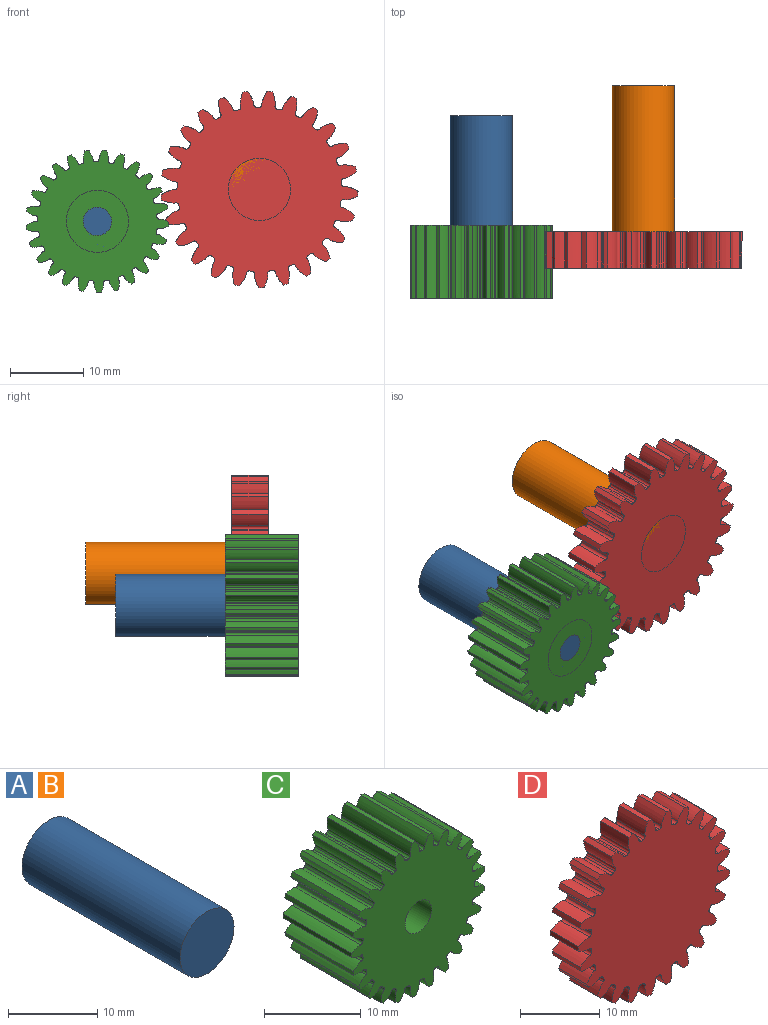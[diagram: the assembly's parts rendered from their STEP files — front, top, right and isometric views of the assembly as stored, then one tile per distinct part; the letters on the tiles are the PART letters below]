
ASSEMBLY  parts=4 mates=2
PART A: 3 faces, bbox 8.5x25x8.5 mm
  f0: cylinder r=4.26mm len=25mm, axis (0,1,0), area 669.3mm2, adj f1,f2
  f1: plane 8.52x8.52mm, normal (0,-1,0), area 57mm2, adj f0
  f2: plane 8.52x8.52mm, normal (0,1,0), area 57mm2, adj f0
PART B: same geometry as A
PART C: 153 faces, bbox 19.5x10x19.6 mm
  f0: cylinder r=9.8mm len=10mm, axis (0,1,0), area 5.2mm2, adj f24,f26,f137,f149
  f1: cylinder r=9.8mm len=10mm, axis (0,1,0), area 5.2mm2, adj f24,f26,f144,f147
  f2: cylinder r=9.8mm len=10mm, axis (0,1,0), area 5.2mm2, adj f24,f26,f132,f139
  f3: cylinder r=9.8mm len=10mm, axis (0,1,0), area 5.2mm2, adj f24,f26,f127,f134
  f4: cylinder r=9.8mm len=10mm, axis (0,1,0), area 5.2mm2, adj f24,f26,f122,f129
  f5: cylinder r=9.8mm len=10mm, axis (0,1,0), area 5.2mm2, adj f24,f26,f112,f124
  f6: cylinder r=9.8mm len=10mm, axis (0,1,0), area 5.2mm2, adj f24,f26,f107,f119
  f7: cylinder r=9.8mm len=10mm, axis (0,1,0), area 5.2mm2, adj f24,f26,f114,f117
  f8: cylinder r=9.8mm len=10mm, axis (0,1,0), area 5.2mm2, adj f24,f26,f102,f109
  f9: cylinder r=9.8mm len=10mm, axis (0,1,0), area 5.2mm2, adj f24,f26,f97,f104
  f10: cylinder r=9.8mm len=10mm, axis (0,1,0), area 5.2mm2, adj f24,f26,f92,f99
  f11: cylinder r=9.8mm len=10mm, axis (0,1,0), area 5.2mm2, adj f24,f26,f77,f94
  f12: cylinder r=9.8mm len=10mm, axis (0,1,0), area 5.2mm2, adj f24,f26,f27,f89
  f13: cylinder r=9.8mm len=10mm, axis (0,1,0), area 5.2mm2, adj f24,f26,f84,f87
  f14: cylinder r=9.8mm len=10mm, axis (0,1,0), area 5.2mm2, adj f24,f26,f72,f79
  f15: cylinder r=9.8mm len=10mm, axis (0,1,0), area 5.2mm2, adj f24,f26,f74,f82
  f16: cylinder r=9.8mm len=10mm, axis (0,1,0), area 5.2mm2, adj f24,f26,f69,f142
  f17: cylinder r=9.8mm len=10mm, axis (0,1,0), area 5.2mm2, adj f24,f26,f64,f67
  f18: cylinder r=9.8mm len=10mm, axis (0,1,0), area 5.2mm2, adj f24,f26,f59,f62
  f19: cylinder r=9.8mm len=10mm, axis (0,1,0), area 5.2mm2, adj f24,f26,f54,f57
  f20: cylinder r=9.8mm len=10mm, axis (0,1,0), area 5.2mm2, adj f24,f26,f42,f49
  f21: cylinder r=9.8mm len=10mm, axis (0,1,0), area 5.2mm2, adj f24,f26,f32,f44
  f22: cylinder r=9.8mm len=10mm, axis (0,1,0), area 5.2mm2, adj f24,f26,f39,f52
  f23: cylinder r=9.8mm len=10mm, axis (0,1,0), area 5.2mm2, adj f24,f26,f34,f37
  f24: plane 19.59x19.55mm, normal (0,-1,0), area 242.9mm2, adj f0,f1,f2,f3,f4,f5,f6,f7
  f25: cylinder r=9.8mm len=10mm, axis (0,1,0), area 5.2mm2, adj f24,f26,f29,f47
  f26: plane 19.59x19.55mm, normal (0,1,0), area 242.9mm2, adj f0,f1,f2,f3,f4,f5,f6,f7
  f27: extruded ~10x1.32mm, area 14.6mm2, adj f12,f24,f26,f30
  f28: cylinder r=8.16mm len=10mm, axis (0,1,0), area 2.5mm2, adj f24,f26,f30,f31
  f29: extruded ~10x1.32mm, area 14.6mm2, adj f24,f25,f26,f31
  f30: cylinder r=0.27mm len=10mm, axis (0,1,0), area 4.2mm2, adj f24,f26,f27,f28
  f31: cylinder r=0.27mm len=10mm, axis (0,1,0), area 4.2mm2, adj f24,f26,f28,f29
  f32: extruded ~10x1.35mm, area 14.6mm2, adj f21,f24,f26,f35
  f33: cylinder r=8.16mm len=10mm, axis (0,1,0), area 2.5mm2, adj f24,f26,f35,f36
  f34: extruded ~10x1.32mm, area 14.6mm2, adj f23,f24,f26,f36
  f35: cylinder r=0.27mm len=10mm, axis (0,1,0), area 4.2mm2, adj f24,f26,f32,f33
  f36: cylinder r=0.27mm len=10mm, axis (0,1,0), area 4.2mm2, adj f24,f26,f33,f34
  f37: extruded ~10x1.19mm, area 14.6mm2, adj f23,f24,f26,f40
  f38: cylinder r=8.16mm len=10mm, axis (0,1,0), area 2.5mm2, adj f24,f26,f40,f41
  f39: extruded ~10x1.42mm, area 14.6mm2, adj f22,f24,f26,f41
  f40: cylinder r=0.27mm len=10mm, axis (0,1,0), area 4.2mm2, adj f24,f26,f37,f38
  f41: cylinder r=0.27mm len=10mm, axis (0,1,0), area 4.2mm2, adj f24,f26,f38,f39
  f42: extruded ~10x1.43mm, area 14.6mm2, adj f20,f24,f26,f45
  f43: cylinder r=8.16mm len=10mm, axis (0,1,0), area 2.5mm2, adj f24,f26,f45,f46
  f44: extruded ~10x1.13mm, area 14.6mm2, adj f21,f24,f26,f46
  f45: cylinder r=0.27mm len=10mm, axis (0,1,0), area 4.2mm2, adj f24,f26,f42,f43
  f46: cylinder r=0.27mm len=10mm, axis (0,1,0), area 4.2mm2, adj f24,f26,f43,f44
  f47: extruded ~10x1.42mm, area 14.6mm2, adj f24,f25,f26,f50
  f48: cylinder r=8.16mm len=10mm, axis (0,1,0), area 2.5mm2, adj f24,f26,f50,f51
  f49: extruded ~10x1.14mm, area 14.6mm2, adj f20,f24,f26,f51
  f50: cylinder r=0.27mm len=10mm, axis (0,1,0), area 4.2mm2, adj f24,f26,f47,f48
  f51: cylinder r=0.27mm len=10mm, axis (0,1,0), area 4.2mm2, adj f24,f26,f48,f49
  f52: extruded ~10x1.09mm, area 14.6mm2, adj f22,f24,f26,f55
  f53: cylinder r=8.16mm len=10mm, axis (0,1,0), area 2.5mm2, adj f24,f26,f55,f56
  f54: extruded ~10x1.43mm, area 14.6mm2, adj f19,f24,f26,f56
  f55: cylinder r=0.27mm len=10mm, axis (0,1,0), area 4.2mm2, adj f24,f26,f52,f53
  f56: cylinder r=0.27mm len=10mm, axis (0,1,0), area 4.2mm2, adj f24,f26,f53,f54
  f57: extruded ~10x1.29mm, area 14.6mm2, adj f19,f24,f26,f60
  f58: cylinder r=8.16mm len=10mm, axis (0,1,0), area 2.5mm2, adj f24,f26,f60,f61
  f59: extruded ~10x1.36mm, area 14.6mm2, adj f18,f24,f26,f61
  f60: cylinder r=0.27mm len=10mm, axis (0,1,0), area 4.2mm2, adj f24,f26,f57,f58
  f61: cylinder r=0.27mm len=10mm, axis (0,1,0), area 4.2mm2, adj f24,f26,f58,f59
  f62: extruded ~10x1.41mm, area 14.6mm2, adj f18,f24,f26,f65
  f63: cylinder r=8.16mm len=10mm, axis (0,1,0), area 2.5mm2, adj f24,f26,f65,f66
  f64: extruded ~10x1.2mm, area 14.6mm2, adj f17,f24,f26,f66
  f65: cylinder r=0.27mm len=10mm, axis (0,1,0), area 4.2mm2, adj f24,f26,f62,f63
  f66: cylinder r=0.27mm len=10mm, axis (0,1,0), area 4.2mm2, adj f24,f26,f63,f64
  f67: extruded ~10x1.44mm, area 14.6mm2, adj f17,f24,f26,f70
  f68: cylinder r=8.16mm len=10mm, axis (0,1,0), area 2.5mm2, adj f24,f26,f70,f71
  f69: extruded ~10x1.08mm, area 14.6mm2, adj f16,f24,f26,f71
  f70: cylinder r=0.27mm len=10mm, axis (0,1,0), area 4.2mm2, adj f24,f26,f67,f68
  f71: cylinder r=0.27mm len=10mm, axis (0,1,0), area 4.2mm2, adj f24,f26,f68,f69
  f72: extruded ~10x1.32mm, area 14.6mm2, adj f14,f24,f26,f75
  f73: cylinder r=8.16mm len=10mm, axis (0,1,0), area 2.5mm2, adj f24,f26,f75,f76
  f74: extruded ~10x1.35mm, area 14.6mm2, adj f15,f24,f26,f76
  f75: cylinder r=0.27mm len=10mm, axis (0,1,0), area 4.2mm2, adj f24,f26,f72,f73
  f76: cylinder r=0.27mm len=10mm, axis (0,1,0), area 4.2mm2, adj f24,f26,f73,f74
  f77: extruded ~10x1.42mm, area 14.6mm2, adj f11,f24,f26,f80
  f78: cylinder r=8.16mm len=10mm, axis (0,1,0), area 2.5mm2, adj f24,f26,f80,f81
  f79: extruded ~10x1.19mm, area 14.6mm2, adj f14,f24,f26,f81
  f80: cylinder r=0.27mm len=10mm, axis (0,1,0), area 4.2mm2, adj f24,f26,f77,f78
  f81: cylinder r=0.27mm len=10mm, axis (0,1,0), area 4.2mm2, adj f24,f26,f78,f79
  f82: extruded ~10x1.13mm, area 14.6mm2, adj f15,f24,f26,f85
  f83: cylinder r=8.16mm len=10mm, axis (0,1,0), area 2.5mm2, adj f24,f26,f85,f86
  f84: extruded ~10x1.43mm, area 14.6mm2, adj f13,f24,f26,f86
  f85: cylinder r=0.27mm len=10mm, axis (0,1,0), area 4.2mm2, adj f24,f26,f82,f83
  f86: cylinder r=0.27mm len=10mm, axis (0,1,0), area 4.2mm2, adj f24,f26,f83,f84
  f87: extruded ~10x1.14mm, area 14.6mm2, adj f13,f24,f26,f90
  f88: cylinder r=8.16mm len=10mm, axis (0,1,0), area 2.5mm2, adj f24,f26,f90,f91
  f89: extruded ~10x1.42mm, area 14.6mm2, adj f12,f24,f26,f91
  f90: cylinder r=0.27mm len=10mm, axis (0,1,0), area 4.2mm2, adj f24,f26,f87,f88
  f91: cylinder r=0.27mm len=10mm, axis (0,1,0), area 4.2mm2, adj f24,f26,f88,f89
  f92: extruded ~10x1.43mm, area 14.6mm2, adj f10,f24,f26,f95
  f93: cylinder r=8.16mm len=10mm, axis (0,1,0), area 2.5mm2, adj f24,f26,f95,f96
  f94: extruded ~10x1.09mm, area 14.6mm2, adj f11,f24,f26,f96
  f95: cylinder r=0.27mm len=10mm, axis (0,1,0), area 4.2mm2, adj f24,f26,f92,f93
  f96: cylinder r=0.27mm len=10mm, axis (0,1,0), area 4.2mm2, adj f24,f26,f93,f94
  f97: extruded ~10x1.36mm, area 14.6mm2, adj f9,f24,f26,f100
  f98: cylinder r=8.16mm len=10mm, axis (0,1,0), area 2.5mm2, adj f24,f26,f100,f101
  f99: extruded ~10x1.29mm, area 14.6mm2, adj f10,f24,f26,f101
  f100: cylinder r=0.27mm len=10mm, axis (0,1,0), area 4.2mm2, adj f24,f26,f97,f98
  f101: cylinder r=0.27mm len=10mm, axis (0,1,0), area 4.2mm2, adj f24,f26,f98,f99
  f102: extruded ~10x1.2mm, area 14.6mm2, adj f8,f24,f26,f105
  f103: cylinder r=8.16mm len=10mm, axis (0,1,0), area 2.5mm2, adj f24,f26,f105,f106
  f104: extruded ~10x1.41mm, area 14.6mm2, adj f9,f24,f26,f106
  f105: cylinder r=0.27mm len=10mm, axis (0,1,0), area 4.2mm2, adj f24,f26,f102,f103
  f106: cylinder r=0.27mm len=10mm, axis (0,1,0), area 4.2mm2, adj f24,f26,f103,f104
  f107: extruded ~10x1.08mm, area 14.6mm2, adj f6,f24,f26,f110
  f108: cylinder r=8.16mm len=10mm, axis (0,1,0), area 2.5mm2, adj f24,f26,f110,f111
  f109: extruded ~10x1.44mm, area 14.6mm2, adj f8,f24,f26,f111
  f110: cylinder r=0.27mm len=10mm, axis (0,1,0), area 4.2mm2, adj f24,f26,f107,f108
  f111: cylinder r=0.27mm len=10mm, axis (0,1,0), area 4.2mm2, adj f24,f26,f108,f109
  f112: extruded ~10x1.4mm, area 14.6mm2, adj f5,f24,f26,f115
  f113: cylinder r=8.16mm len=10mm, axis (0,1,0), area 2.5mm2, adj f24,f26,f115,f116
  f114: extruded ~10x1.24mm, area 14.6mm2, adj f7,f24,f26,f116
  f115: cylinder r=0.27mm len=10mm, axis (0,1,0), area 4.2mm2, adj f24,f26,f112,f113
  f116: cylinder r=0.27mm len=10mm, axis (0,1,0), area 4.2mm2, adj f24,f26,f113,f114
  f117: extruded ~10x1.28mm, area 14.6mm2, adj f7,f24,f26,f120
  f118: cylinder r=8.16mm len=10mm, axis (0,1,0), area 2.5mm2, adj f24,f26,f120,f121
  f119: extruded ~10x1.38mm, area 14.6mm2, adj f6,f24,f26,f121
  f120: cylinder r=0.27mm len=10mm, axis (0,1,0), area 4.2mm2, adj f24,f26,f117,f118
  f121: cylinder r=0.27mm len=10mm, axis (0,1,0), area 4.2mm2, adj f24,f26,f118,f119
  f122: extruded ~10x1.44mm, area 14.6mm2, adj f4,f24,f26,f125
  f123: cylinder r=8.16mm len=10mm, axis (0,1,0), area 2.5mm2, adj f24,f26,f125,f126
  f124: extruded ~10x1.02mm, area 14.6mm2, adj f5,f24,f26,f126
  f125: cylinder r=0.27mm len=10mm, axis (0,1,0), area 4.2mm2, adj f24,f26,f122,f123
  f126: cylinder r=0.27mm len=10mm, axis (0,1,0), area 4.2mm2, adj f24,f26,f123,f124
  f127: extruded ~10x1.39mm, area 14.6mm2, adj f3,f24,f26,f130
  f128: cylinder r=8.16mm len=10mm, axis (0,1,0), area 2.5mm2, adj f24,f26,f130,f131
  f129: extruded ~10x1.24mm, area 14.6mm2, adj f4,f24,f26,f131
  f130: cylinder r=0.27mm len=10mm, axis (0,1,0), area 4.2mm2, adj f24,f26,f127,f128
  f131: cylinder r=0.27mm len=10mm, axis (0,1,0), area 4.2mm2, adj f24,f26,f128,f129
  f132: extruded ~10x1.24mm, area 14.6mm2, adj f2,f24,f26,f135
  f133: cylinder r=8.16mm len=10mm, axis (0,1,0), area 2.5mm2, adj f24,f26,f135,f136
  f134: extruded ~10x1.39mm, area 14.6mm2, adj f3,f24,f26,f136
  f135: cylinder r=0.27mm len=10mm, axis (0,1,0), area 4.2mm2, adj f24,f26,f132,f133
  f136: cylinder r=0.27mm len=10mm, axis (0,1,0), area 4.2mm2, adj f24,f26,f133,f134
  f137: extruded ~10x1.02mm, area 14.6mm2, adj f0,f24,f26,f140
  f138: cylinder r=8.16mm len=10mm, axis (0,1,0), area 2.5mm2, adj f24,f26,f140,f141
  f139: extruded ~10x1.44mm, area 14.6mm2, adj f2,f24,f26,f141
  f140: cylinder r=0.27mm len=10mm, axis (0,1,0), area 4.2mm2, adj f24,f26,f137,f138
  f141: cylinder r=0.27mm len=10mm, axis (0,1,0), area 4.2mm2, adj f24,f26,f138,f139
  f142: extruded ~10x1.38mm, area 14.6mm2, adj f16,f24,f26,f145
  f143: cylinder r=8.16mm len=10mm, axis (0,1,0), area 2.5mm2, adj f24,f26,f145,f146
  f144: extruded ~10x1.28mm, area 14.6mm2, adj f1,f24,f26,f146
  f145: cylinder r=0.27mm len=10mm, axis (0,1,0), area 4.2mm2, adj f24,f26,f142,f143
  f146: cylinder r=0.27mm len=10mm, axis (0,1,0), area 4.2mm2, adj f24,f26,f143,f144
  f147: extruded ~10x1.24mm, area 14.6mm2, adj f1,f24,f26,f150
  f148: cylinder r=8.16mm len=10mm, axis (0,1,0), area 2.5mm2, adj f24,f26,f150,f151
  f149: extruded ~10x1.4mm, area 14.6mm2, adj f0,f24,f26,f151
  f150: cylinder r=0.27mm len=10mm, axis (0,1,0), area 4.2mm2, adj f24,f26,f147,f148
  f151: cylinder r=0.27mm len=10mm, axis (0,1,0), area 4.2mm2, adj f24,f26,f148,f149
  f152: cylinder r=1.94mm len=10mm, axis (0,-1,0), area 122mm2, adj f24,f26
PART D: 152 faces, bbox 26.9x5x27 mm
  f0: cylinder r=13.5mm len=5mm, axis (0,1,0), area 3.6mm2, adj f24,f26,f137,f149
  f1: cylinder r=13.5mm len=5mm, axis (0,1,0), area 3.6mm2, adj f24,f26,f144,f147
  f2: cylinder r=13.5mm len=5mm, axis (0,1,0), area 3.6mm2, adj f24,f26,f132,f139
  f3: cylinder r=13.5mm len=5mm, axis (0,1,0), area 3.6mm2, adj f24,f26,f127,f134
  f4: cylinder r=13.5mm len=5mm, axis (0,1,0), area 3.6mm2, adj f24,f26,f122,f129
  f5: cylinder r=13.5mm len=5mm, axis (0,1,0), area 3.6mm2, adj f24,f26,f112,f124
  f6: cylinder r=13.5mm len=5mm, axis (0,1,0), area 3.6mm2, adj f24,f26,f107,f119
  f7: cylinder r=13.5mm len=5mm, axis (0,1,0), area 3.6mm2, adj f24,f26,f114,f117
  f8: cylinder r=13.5mm len=5mm, axis (0,1,0), area 3.6mm2, adj f24,f26,f102,f109
  f9: cylinder r=13.5mm len=5mm, axis (0,1,0), area 3.6mm2, adj f24,f26,f97,f104
  f10: cylinder r=13.5mm len=5mm, axis (0,1,0), area 3.6mm2, adj f24,f26,f92,f99
  f11: cylinder r=13.5mm len=5mm, axis (0,1,0), area 3.6mm2, adj f24,f26,f77,f94
  f12: cylinder r=13.5mm len=5mm, axis (0,1,0), area 3.6mm2, adj f24,f26,f27,f89
  f13: cylinder r=13.5mm len=5mm, axis (0,1,0), area 3.6mm2, adj f24,f26,f84,f87
  f14: cylinder r=13.5mm len=5mm, axis (0,1,0), area 3.6mm2, adj f24,f26,f72,f79
  f15: cylinder r=13.5mm len=5mm, axis (0,1,0), area 3.6mm2, adj f24,f26,f74,f82
  f16: cylinder r=13.5mm len=5mm, axis (0,1,0), area 3.6mm2, adj f24,f26,f69,f142
  f17: cylinder r=13.5mm len=5mm, axis (0,1,0), area 3.6mm2, adj f24,f26,f64,f67
  f18: cylinder r=13.5mm len=5mm, axis (0,1,0), area 3.6mm2, adj f24,f26,f59,f62
  f19: cylinder r=13.5mm len=5mm, axis (0,1,0), area 3.6mm2, adj f24,f26,f54,f57
  f20: cylinder r=13.5mm len=5mm, axis (0,1,0), area 3.6mm2, adj f24,f26,f42,f49
  f21: cylinder r=13.5mm len=5mm, axis (0,1,0), area 3.6mm2, adj f24,f26,f32,f44
  f22: cylinder r=13.5mm len=5mm, axis (0,1,0), area 3.6mm2, adj f24,f26,f39,f52
  f23: cylinder r=13.5mm len=5mm, axis (0,1,0), area 3.6mm2, adj f24,f26,f34,f37
  f24: plane 26.99x26.94mm, normal (0,-1,0), area 483.6mm2, adj f0,f1,f2,f3,f4,f5,f6,f7
  f25: cylinder r=13.5mm len=5mm, axis (0,1,0), area 3.6mm2, adj f24,f26,f29,f47
  f26: plane 26.99x26.94mm, normal (0,1,0), area 483.6mm2, adj f0,f1,f2,f3,f4,f5,f6,f7
  f27: extruded ~5x1.83mm, area 10mm2, adj f12,f24,f26,f30
  f28: cylinder r=11.25mm len=5mm, axis (0,1,0), area 1.7mm2, adj f24,f26,f30,f31
  f29: extruded ~5x1.83mm, area 10mm2, adj f24,f25,f26,f31
  f30: cylinder r=0.38mm len=5mm, axis (0,1,0), area 2.9mm2, adj f24,f26,f27,f28
  f31: cylinder r=0.38mm len=5mm, axis (0,1,0), area 2.9mm2, adj f24,f26,f28,f29
  f32: extruded ~5x1.86mm, area 10mm2, adj f21,f24,f26,f35
  f33: cylinder r=11.25mm len=5mm, axis (0,1,0), area 1.7mm2, adj f24,f26,f35,f36
  f34: extruded ~5x1.82mm, area 10mm2, adj f23,f24,f26,f36
  f35: cylinder r=0.38mm len=5mm, axis (0,1,0), area 2.9mm2, adj f24,f26,f32,f33
  f36: cylinder r=0.38mm len=5mm, axis (0,1,0), area 2.9mm2, adj f24,f26,f33,f34
  f37: extruded ~5x1.64mm, area 10mm2, adj f23,f24,f26,f40
  f38: cylinder r=11.25mm len=5mm, axis (0,1,0), area 1.7mm2, adj f24,f26,f40,f41
  f39: extruded ~5x1.96mm, area 10mm2, adj f22,f24,f26,f41
  f40: cylinder r=0.38mm len=5mm, axis (0,1,0), area 2.9mm2, adj f24,f26,f37,f38
  f41: cylinder r=0.38mm len=5mm, axis (0,1,0), area 2.9mm2, adj f24,f26,f38,f39
  f42: extruded ~5x1.98mm, area 10mm2, adj f20,f24,f26,f45
  f43: cylinder r=11.25mm len=5mm, axis (0,1,0), area 1.7mm2, adj f24,f26,f45,f46
  f44: extruded ~5x1.56mm, area 10mm2, adj f21,f24,f26,f46
  f45: cylinder r=0.38mm len=5mm, axis (0,1,0), area 2.9mm2, adj f24,f26,f42,f43
  f46: cylinder r=0.38mm len=5mm, axis (0,1,0), area 2.9mm2, adj f24,f26,f43,f44
  f47: extruded ~5x1.96mm, area 10mm2, adj f24,f25,f26,f50
  f48: cylinder r=11.25mm len=5mm, axis (0,1,0), area 1.7mm2, adj f24,f26,f50,f51
  f49: extruded ~5x1.57mm, area 10mm2, adj f20,f24,f26,f51
  f50: cylinder r=0.38mm len=5mm, axis (0,1,0), area 2.9mm2, adj f24,f26,f47,f48
  f51: cylinder r=0.38mm len=5mm, axis (0,1,0), area 2.9mm2, adj f24,f26,f48,f49
  f52: extruded ~5x1.5mm, area 10mm2, adj f22,f24,f26,f55
  f53: cylinder r=11.25mm len=5mm, axis (0,1,0), area 1.7mm2, adj f24,f26,f55,f56
  f54: extruded ~5x1.98mm, area 10mm2, adj f19,f24,f26,f56
  f55: cylinder r=0.38mm len=5mm, axis (0,1,0), area 2.9mm2, adj f24,f26,f52,f53
  f56: cylinder r=0.38mm len=5mm, axis (0,1,0), area 2.9mm2, adj f24,f26,f53,f54
  f57: extruded ~5x1.77mm, area 10mm2, adj f19,f24,f26,f60
  f58: cylinder r=11.25mm len=5mm, axis (0,1,0), area 1.7mm2, adj f24,f26,f60,f61
  f59: extruded ~5x1.87mm, area 10mm2, adj f18,f24,f26,f61
  f60: cylinder r=0.38mm len=5mm, axis (0,1,0), area 2.9mm2, adj f24,f26,f57,f58
  f61: cylinder r=0.38mm len=5mm, axis (0,1,0), area 2.9mm2, adj f24,f26,f58,f59
  f62: extruded ~5x1.94mm, area 10mm2, adj f18,f24,f26,f65
  f63: cylinder r=11.25mm len=5mm, axis (0,1,0), area 1.7mm2, adj f24,f26,f65,f66
  f64: extruded ~5x1.65mm, area 10mm2, adj f17,f24,f26,f66
  f65: cylinder r=0.38mm len=5mm, axis (0,1,0), area 2.9mm2, adj f24,f26,f62,f63
  f66: cylinder r=0.38mm len=5mm, axis (0,1,0), area 2.9mm2, adj f24,f26,f63,f64
  f67: extruded ~5x1.98mm, area 10mm2, adj f17,f24,f26,f70
  f68: cylinder r=11.25mm len=5mm, axis (0,1,0), area 1.7mm2, adj f24,f26,f70,f71
  f69: extruded ~5x1.48mm, area 10mm2, adj f16,f24,f26,f71
  f70: cylinder r=0.38mm len=5mm, axis (0,1,0), area 2.9mm2, adj f24,f26,f67,f68
  f71: cylinder r=0.38mm len=5mm, axis (0,1,0), area 2.9mm2, adj f24,f26,f68,f69
  f72: extruded ~5x1.82mm, area 10mm2, adj f14,f24,f26,f75
  f73: cylinder r=11.25mm len=5mm, axis (0,1,0), area 1.7mm2, adj f24,f26,f75,f76
  f74: extruded ~5x1.86mm, area 10mm2, adj f15,f24,f26,f76
  f75: cylinder r=0.38mm len=5mm, axis (0,1,0), area 2.9mm2, adj f24,f26,f72,f73
  f76: cylinder r=0.38mm len=5mm, axis (0,1,0), area 2.9mm2, adj f24,f26,f73,f74
  f77: extruded ~5x1.96mm, area 10mm2, adj f11,f24,f26,f80
  f78: cylinder r=11.25mm len=5mm, axis (0,1,0), area 1.7mm2, adj f24,f26,f80,f81
  f79: extruded ~5x1.64mm, area 10mm2, adj f14,f24,f26,f81
  f80: cylinder r=0.38mm len=5mm, axis (0,1,0), area 2.9mm2, adj f24,f26,f77,f78
  f81: cylinder r=0.38mm len=5mm, axis (0,1,0), area 2.9mm2, adj f24,f26,f78,f79
  f82: extruded ~5x1.56mm, area 10mm2, adj f15,f24,f26,f85
  f83: cylinder r=11.25mm len=5mm, axis (0,1,0), area 1.7mm2, adj f24,f26,f85,f86
  f84: extruded ~5x1.98mm, area 10mm2, adj f13,f24,f26,f86
  f85: cylinder r=0.38mm len=5mm, axis (0,1,0), area 2.9mm2, adj f24,f26,f82,f83
  f86: cylinder r=0.38mm len=5mm, axis (0,1,0), area 2.9mm2, adj f24,f26,f83,f84
  f87: extruded ~5x1.57mm, area 10mm2, adj f13,f24,f26,f90
  f88: cylinder r=11.25mm len=5mm, axis (0,1,0), area 1.7mm2, adj f24,f26,f90,f91
  f89: extruded ~5x1.96mm, area 10mm2, adj f12,f24,f26,f91
  f90: cylinder r=0.38mm len=5mm, axis (0,1,0), area 2.9mm2, adj f24,f26,f87,f88
  f91: cylinder r=0.38mm len=5mm, axis (0,1,0), area 2.9mm2, adj f24,f26,f88,f89
  f92: extruded ~5x1.98mm, area 10mm2, adj f10,f24,f26,f95
  f93: cylinder r=11.25mm len=5mm, axis (0,1,0), area 1.7mm2, adj f24,f26,f95,f96
  f94: extruded ~5x1.5mm, area 10mm2, adj f11,f24,f26,f96
  f95: cylinder r=0.38mm len=5mm, axis (0,1,0), area 2.9mm2, adj f24,f26,f92,f93
  f96: cylinder r=0.38mm len=5mm, axis (0,1,0), area 2.9mm2, adj f24,f26,f93,f94
  f97: extruded ~5x1.87mm, area 10mm2, adj f9,f24,f26,f100
  f98: cylinder r=11.25mm len=5mm, axis (0,1,0), area 1.7mm2, adj f24,f26,f100,f101
  f99: extruded ~5x1.77mm, area 10mm2, adj f10,f24,f26,f101
  f100: cylinder r=0.38mm len=5mm, axis (0,1,0), area 2.9mm2, adj f24,f26,f97,f98
  f101: cylinder r=0.38mm len=5mm, axis (0,1,0), area 2.9mm2, adj f24,f26,f98,f99
  f102: extruded ~5x1.65mm, area 10mm2, adj f8,f24,f26,f105
  f103: cylinder r=11.25mm len=5mm, axis (0,1,0), area 1.7mm2, adj f24,f26,f105,f106
  f104: extruded ~5x1.94mm, area 10mm2, adj f9,f24,f26,f106
  f105: cylinder r=0.38mm len=5mm, axis (0,1,0), area 2.9mm2, adj f24,f26,f102,f103
  f106: cylinder r=0.38mm len=5mm, axis (0,1,0), area 2.9mm2, adj f24,f26,f103,f104
  f107: extruded ~5x1.48mm, area 10mm2, adj f6,f24,f26,f110
  f108: cylinder r=11.25mm len=5mm, axis (0,1,0), area 1.7mm2, adj f24,f26,f110,f111
  f109: extruded ~5x1.98mm, area 10mm2, adj f8,f24,f26,f111
  f110: cylinder r=0.38mm len=5mm, axis (0,1,0), area 2.9mm2, adj f24,f26,f107,f108
  f111: cylinder r=0.38mm len=5mm, axis (0,1,0), area 2.9mm2, adj f24,f26,f108,f109
  f112: extruded ~5x1.93mm, area 10mm2, adj f5,f24,f26,f115
  f113: cylinder r=11.25mm len=5mm, axis (0,1,0), area 1.7mm2, adj f24,f26,f115,f116
  f114: extruded ~5x1.7mm, area 10mm2, adj f7,f24,f26,f116
  f115: cylinder r=0.38mm len=5mm, axis (0,1,0), area 2.9mm2, adj f24,f26,f112,f113
  f116: cylinder r=0.38mm len=5mm, axis (0,1,0), area 2.9mm2, adj f24,f26,f113,f114
  f117: extruded ~5x1.76mm, area 10mm2, adj f7,f24,f26,f120
  f118: cylinder r=11.25mm len=5mm, axis (0,1,0), area 1.7mm2, adj f24,f26,f120,f121
  f119: extruded ~5x1.9mm, area 10mm2, adj f6,f24,f26,f121
  f120: cylinder r=0.38mm len=5mm, axis (0,1,0), area 2.9mm2, adj f24,f26,f117,f118
  f121: cylinder r=0.38mm len=5mm, axis (0,1,0), area 2.9mm2, adj f24,f26,f118,f119
  f122: extruded ~5x1.98mm, area 10mm2, adj f4,f24,f26,f125
  f123: cylinder r=11.25mm len=5mm, axis (0,1,0), area 1.7mm2, adj f24,f26,f125,f126
  f124: extruded ~5x1.41mm, area 10mm2, adj f5,f24,f26,f126
  f125: cylinder r=0.38mm len=5mm, axis (0,1,0), area 2.9mm2, adj f24,f26,f122,f123
  f126: cylinder r=0.38mm len=5mm, axis (0,1,0), area 2.9mm2, adj f24,f26,f123,f124
  f127: extruded ~5x1.91mm, area 10mm2, adj f3,f24,f26,f130
  f128: cylinder r=11.25mm len=5mm, axis (0,1,0), area 1.7mm2, adj f24,f26,f130,f131
  f129: extruded ~5x1.71mm, area 10mm2, adj f4,f24,f26,f131
  f130: cylinder r=0.38mm len=5mm, axis (0,1,0), area 2.9mm2, adj f24,f26,f127,f128
  f131: cylinder r=0.38mm len=5mm, axis (0,1,0), area 2.9mm2, adj f24,f26,f128,f129
  f132: extruded ~5x1.71mm, area 10mm2, adj f2,f24,f26,f135
  f133: cylinder r=11.25mm len=5mm, axis (0,1,0), area 1.7mm2, adj f24,f26,f135,f136
  f134: extruded ~5x1.91mm, area 10mm2, adj f3,f24,f26,f136
  f135: cylinder r=0.38mm len=5mm, axis (0,1,0), area 2.9mm2, adj f24,f26,f132,f133
  f136: cylinder r=0.38mm len=5mm, axis (0,1,0), area 2.9mm2, adj f24,f26,f133,f134
  f137: extruded ~5x1.41mm, area 10mm2, adj f0,f24,f26,f140
  f138: cylinder r=11.25mm len=5mm, axis (0,1,0), area 1.7mm2, adj f24,f26,f140,f141
  f139: extruded ~5x1.98mm, area 10mm2, adj f2,f24,f26,f141
  f140: cylinder r=0.38mm len=5mm, axis (0,1,0), area 2.9mm2, adj f24,f26,f137,f138
  f141: cylinder r=0.38mm len=5mm, axis (0,1,0), area 2.9mm2, adj f24,f26,f138,f139
  f142: extruded ~5x1.9mm, area 10mm2, adj f16,f24,f26,f145
  f143: cylinder r=11.25mm len=5mm, axis (0,1,0), area 1.7mm2, adj f24,f26,f145,f146
  f144: extruded ~5x1.76mm, area 10mm2, adj f1,f24,f26,f146
  f145: cylinder r=0.38mm len=5mm, axis (0,1,0), area 2.9mm2, adj f24,f26,f142,f143
  f146: cylinder r=0.38mm len=5mm, axis (0,1,0), area 2.9mm2, adj f24,f26,f143,f144
  f147: extruded ~5x1.7mm, area 10mm2, adj f1,f24,f26,f150
  f148: cylinder r=11.25mm len=5mm, axis (0,1,0), area 1.7mm2, adj f24,f26,f150,f151
  f149: extruded ~5x1.93mm, area 10mm2, adj f0,f24,f26,f151
  f150: cylinder r=0.38mm len=5mm, axis (0,1,0), area 2.9mm2, adj f24,f26,f147,f148
  f151: cylinder r=0.38mm len=5mm, axis (0,1,0), area 2.9mm2, adj f24,f26,f148,f149
PLACE A t=(-67.12,15.88,51.22)mm fixed
PLACE B t=(-44.93,19.99,55.6)mm fixed
PLACE C rot(axis=(0,-1,0),76.9deg) t=(-22.26,0.88,-3.93)mm
PLACE D rot(axis=(0,1,0),96.1deg) t=(-0.07,-0.01,0.44)mm
MATE revolute A.f0 <-> C.f0  axis (0,-1,0) through (-22.26,-9.12,-3.93)mm
MATE revolute B.f0 <-> D.f0  axis (0,-1,0) through (-0.07,-5.01,0.44)mm
